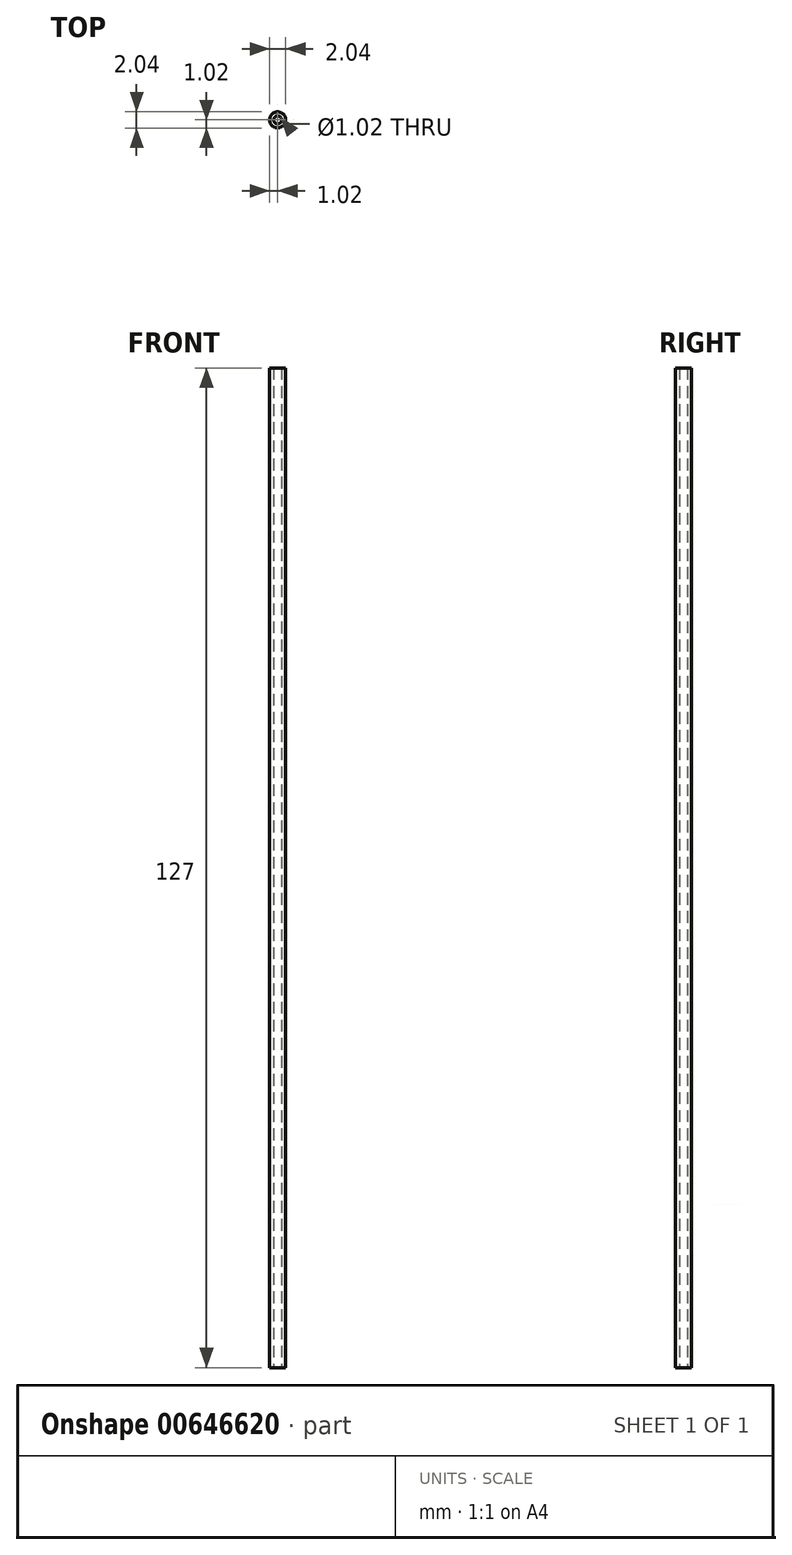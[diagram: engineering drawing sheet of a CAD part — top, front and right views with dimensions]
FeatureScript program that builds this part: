
annotation { "Feature Type Name" : "Feature", "Feature Type Description" : "" }
export const myFeature = defineFeature(function(context is Context, id is Id, definition is map)
    precondition{}
    {
        {
            var Q0;
            Q0=qCreatedBy(makeId("Top.planeOp"),FACE);
            var sketch = newSketch(context, id + "F0", { "sketchPlane" : qUnion([Q0])});
            skCircle(sketch, "E0", {"center": v(0, 0) * mm, "radius": 1.02 * mm});
            skCircle(sketch, "E1", {"center": v(0, 0) * mm, "radius": 0.5 * mm});
            skSolve(sketch);
        }
        {
            var Q0;
            Q0=makeQuery(id+"F0.imprint","IMPRINT",FACE,{"disambiguationData":[TD([[makeQuery(id+"F0.imprint","IMPRINT",EDGE,{"derivedFrom":sQuery(id+"F0.wireOp",EDGE,"E0")}),1.0]])]});
            extrude(context, id + "F1", {"entities" : qUnion([Q0]), "depth" : 127 * mm, "offsetDistance" : 25.4 * mm});
        }
    });
